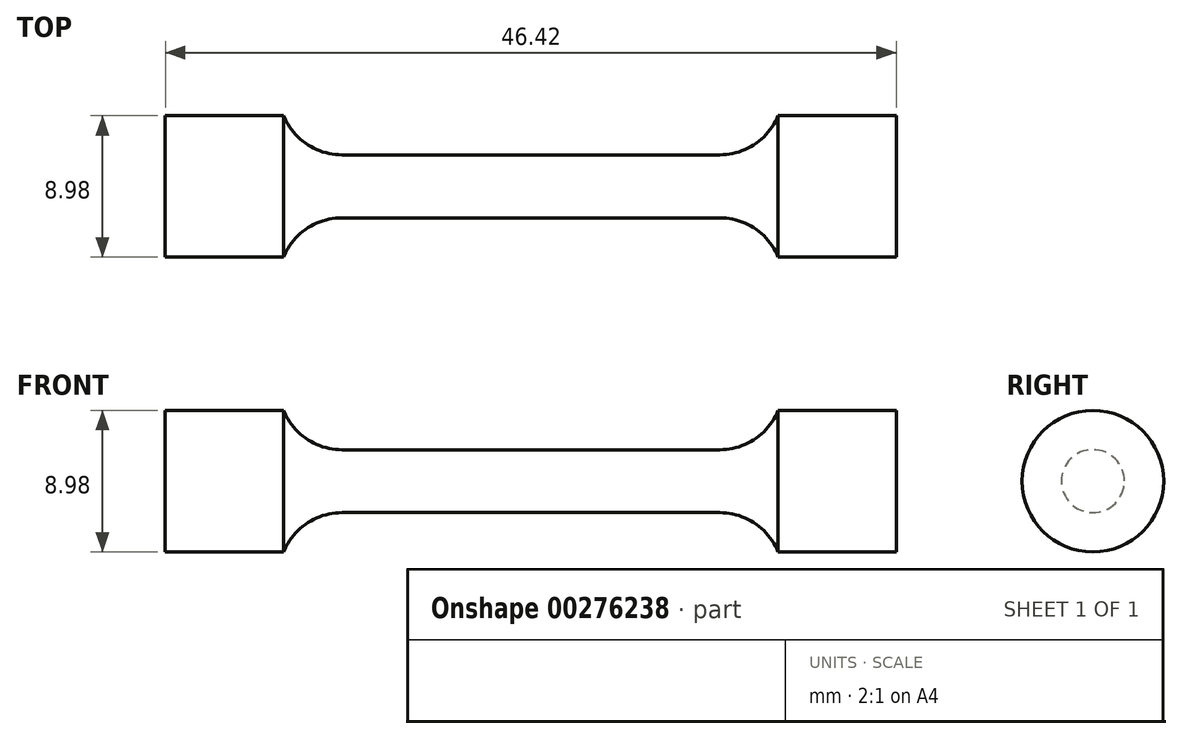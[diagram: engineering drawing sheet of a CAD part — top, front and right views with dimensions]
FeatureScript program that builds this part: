
annotation { "Feature Type Name" : "Feature", "Feature Type Description" : "" }
export const myFeature = defineFeature(function(context is Context, id is Id, definition is map)
    precondition{}
    {
        {
            var Q0;
            Q0=qCreatedBy(makeId("Front.planeOp"),FACE);
            var sketch = newSketch(context, id + "F0", { "sketchPlane" : qUnion([Q0])});
            skLineSegment(sketch, "E0", {"start": v(0, 2) * mm, "end": v(12, 2) * mm});
            skArc(sketch, "E1", {"start": v(12, 2) * mm, "mid": v(14.23, 2.68) * mm, "end": v(15.7, 4.5) * mm});
            skLineSegment(sketch, "E2", {"start": v(15.7, 4.5) * mm, "end": v(23.21, 4.5) * mm});
            skLineSegment(sketch, "E3", {"start": v(23.21, 4.5) * mm, "end": v(23.21, 0) * mm});
            skLineSegment(sketch, "E4", {"start": v(23.21, 0) * mm, "end": v(0, 0) * mm});
            skLineSegment(sketch, "E5.MirrorCS", {"start": v(-15.7, 4.5) * mm, "end": v(-23.21, 4.5) * mm});
            skLineSegment(sketch, "E6.MirrorCS", {"start": v(0, 2) * mm, "end": v(-12, 2) * mm});
            skLineSegment(sketch, "E7.MirrorCS", {"start": v(-23.21, 4.5) * mm, "end": v(-23.21, 0) * mm});
            skLineSegment(sketch, "E8.MirrorCS", {"start": v(-23.21, 0) * mm, "end": v(0, 0) * mm});
            skArc(sketch, "E9.MirrorCS", {"start": v(-12, 2) * mm, "mid": v(-14.23, 2.68) * mm, "end": v(-15.7, 4.5) * mm});
            skSolve(sketch);
        }
        {
            var Q0;
            Q0 = qSketchRegion(id + "F0", true);
            var Q1;
            Q1=sQuery(id+"F0.wireOp",EDGE,"E8.MirrorCS");
            revolve(context, id + "F1", {"entities" : qUnion([Q0]), "axis" : qUnion([Q1]), "revolveType" : RevolveType.FULL});
        }
    });
